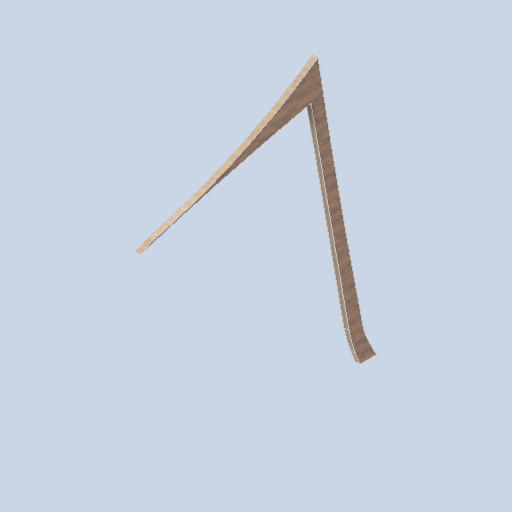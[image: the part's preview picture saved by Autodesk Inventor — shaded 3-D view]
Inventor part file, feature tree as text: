
AUTODESK INVENTOR PART (.ipt)
format: ipt  version: 2024.2 (Build 282272000, 272)  size: 302,080 bytes
history: native  units: in
note: dims shown in document units (in); Inventor stores cm internally (conversion verified against a paired STEP export)
features: other x3, fillet x1, sketch x1
ambient origin geometry x8: Origin, YZ Plane, XZ Plane, XY Plane, X Axis, Y Axis, Z Axis, Center Point
bodies: Body1 (feature_tree)
feature tree (5):
  other  "side_curve_beam_01.ipt"
  fillet  "Fillet1"  Radius=0.3937in
  other  "Solid2::side_curve_beam_01.ipt"
  other  "TaggingFeature1"
  sketch  "Sketch1"  dims[d1=0.3937in]
